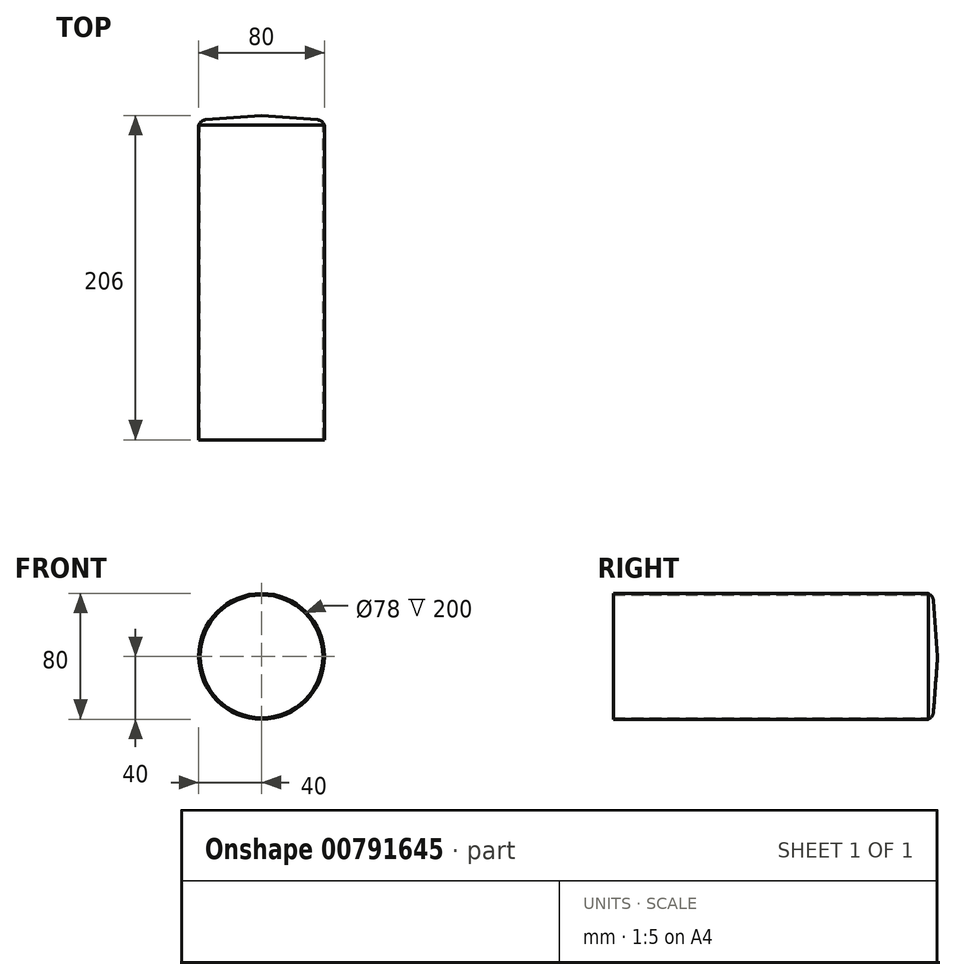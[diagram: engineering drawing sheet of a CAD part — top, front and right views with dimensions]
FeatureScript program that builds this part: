
annotation { "Feature Type Name" : "Feature", "Feature Type Description" : "" }
export const myFeature = defineFeature(function(context is Context, id is Id, definition is map)
    precondition{}
    {
        {
            var Q0;
            Q0=qCreatedBy(makeId("Front.planeOp"),FACE);
            var sketch = newSketch(context, id + "F0", { "sketchPlane" : qUnion([Q0])});
            skCircle(sketch, "E0", {"center": v(0, 0) * mm, "radius": 40 * mm});
            skCircle(sketch, "E1", {"center": v(0, 0) * mm, "radius": 39 * mm});
            skSolve(sketch);
        }
        {
            var Q0;
            Q0=makeQuery(id+"F0.imprint","IMPRINT",FACE,{"disambiguationData":[TD([[makeQuery(id+"F0.imprint","IMPRINT",EDGE,{"derivedFrom":sQuery(id+"F0.wireOp",EDGE,"E0")}),1.0]])]});
            extrude(context, id + "F1", {"entities" : qUnion([Q0]), "depth" : 200 * mm, "offsetDistance" : 25 * mm});
        }
        {
            var Q0;
            Q0=qCreatedBy(makeId("Right.planeOp"),FACE);
            var sketch = newSketch(context, id + "F2", { "sketchPlane" : qUnion([Q0])});
            skLineSegment(sketch, "E2", {"start": v(0, -39.83) * mm, "end": v(3, -39.83) * mm});
            skLineSegment(sketch, "E3", {"start": v(3, -39.83) * mm, "end": v(6, 0) * mm});
            skLineSegment(sketch, "E4", {"start": v(6, 0) * mm, "end": v(0, 0) * mm});
            skLineSegment(sketch, "E5", {"start": v(0, 0) * mm, "end": v(0, -39.83) * mm});
            skSolve(sketch);
        }
        {
            var Q0;
            Q0=makeQuery(id+"F2.imprint","IMPRINT",FACE,{"disambiguationData":[TD([[makeQuery(id+"F2.imprint","IMPRINT",EDGE,{"derivedFrom":sQuery(id+"F2.wireOp",EDGE,"E2")}),1.0]])]});
            var Q1;
            Q1=sQuery(id+"F2.wireOp",EDGE,"E4");
            revolve(context, id + "F3", {"operationType" : NewBodyOperationType.ADD, "surfaceOperationType" : NewSurfaceOperationType.NEW, "entities" : qUnion([Q0]), "axis" : qUnion([Q1]), "revolveType" : RevolveType.FULL});
        }
        {
            var Q0;
            Q0=makeQuery(id+"F3.opRevolve","SWEPT_EDGE",EDGE,{"disambiguationData":[OSD([sQuery(id+"F2.wireOp",EDGE,"E2"),sQuery(id+"F2.wireOp",EDGE,"E3")])]});
            fillet(context, id + "F4", {"entities" : qUnion([Q0]), "radius" : 5 * mm, "tangentPropagation" : true, "allowEdgeOverflow" : false});
        }
    });
